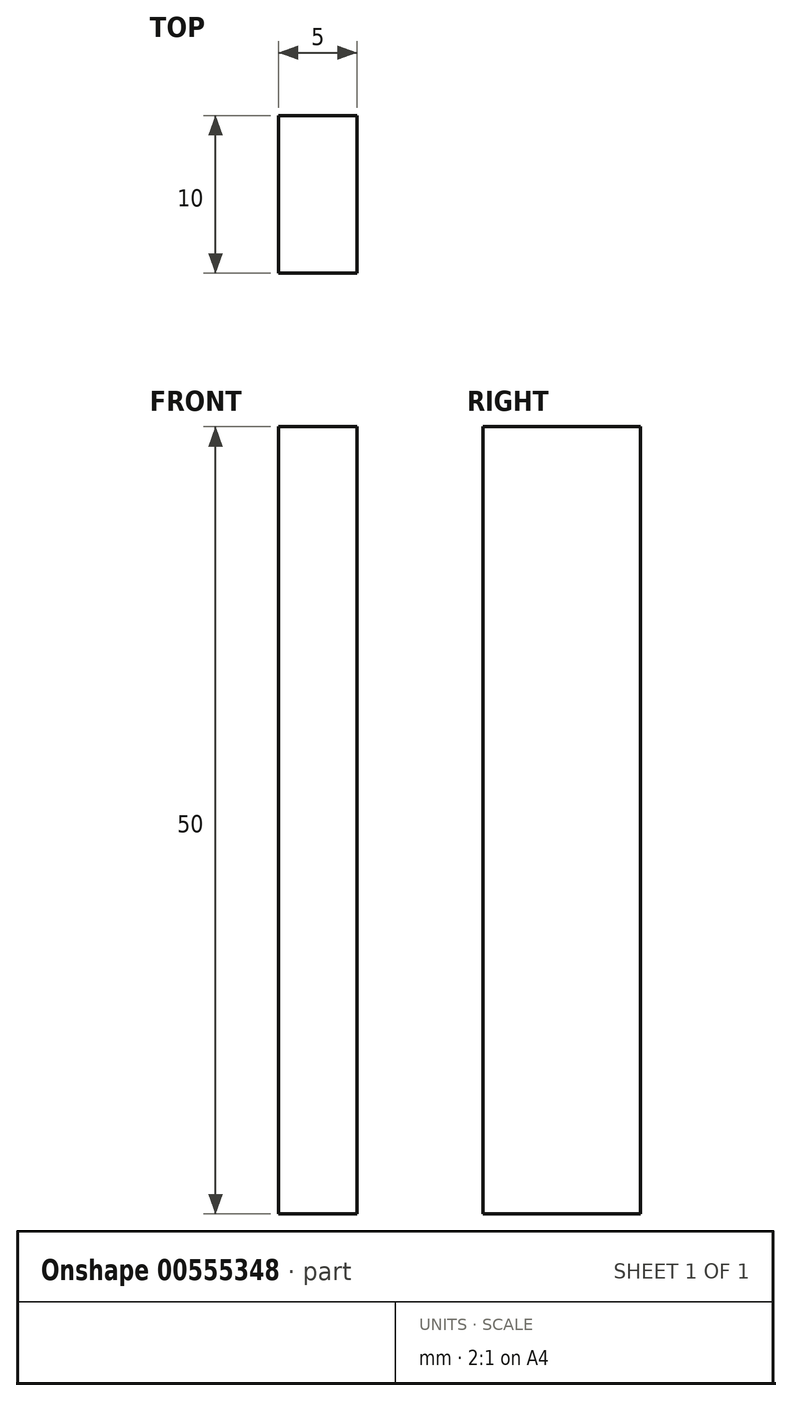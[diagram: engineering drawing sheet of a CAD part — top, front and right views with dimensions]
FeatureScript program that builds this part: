
annotation { "Feature Type Name" : "Feature", "Feature Type Description" : "" }
export const myFeature = defineFeature(function(context is Context, id is Id, definition is map)
    precondition{}
    {
        {
            var Q0;
            Q0=qCreatedBy(makeId("Front.planeOp"),FACE);
            var sketch = newSketch(context, id + "F0", { "sketchPlane" : qUnion([Q0])});
            skLineSegment(sketch, "E0", {"start": v(-63.83, 50) * mm, "end": v(-63.83, 0) * mm});
            skLineSegment(sketch, "E1", {"start": v(-63.83, 0) * mm, "end": v(-58.83, 0) * mm});
            skLineSegment(sketch, "E2", {"start": v(-58.83, 0) * mm, "end": v(-58.83, 50) * mm});
            skLineSegment(sketch, "E3", {"start": v(-58.83, 50) * mm, "end": v(-63.83, 50) * mm});
            skSolve(sketch);
        }
        {
            var Q0;
            Q0=makeQuery(id+"F0.imprint","IMPRINT",FACE,{"disambiguationData":[TD([[makeQuery(id+"F0.imprint","IMPRINT",EDGE,{"derivedFrom":sQuery(id+"F0.wireOp",EDGE,"E0")}),1.0]])]});
            extrude(context, id + "F1", {"entities" : qUnion([Q0]), "depth" : 10 * mm, "offsetDistance" : 25 * mm});
        }
    });
